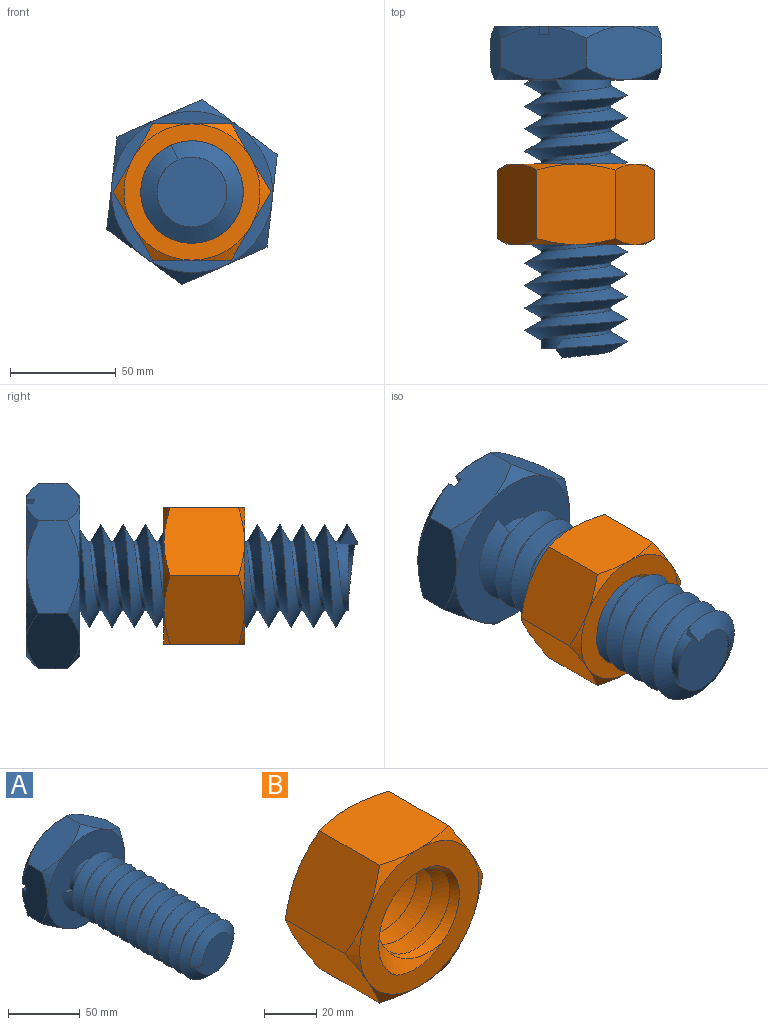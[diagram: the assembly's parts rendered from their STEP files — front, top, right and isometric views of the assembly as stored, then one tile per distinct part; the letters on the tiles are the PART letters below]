
ASSEMBLY  parts=2 mates=1
PART A: 22 faces, bbox 88x156.9x88 mm
  f0: plane 44.01x25.33mm, normal (1,0,0), area 920.4mm2, adj f2,f12,f14,f15,f17,f19,f20,f21
  f1: plane 44.01x25.33mm, normal (-1,0,0), area 920.4mm2, adj f2,f12,f13,f16,f17,f19,f20,f21
  f2: cone r=48.09mm half-angle=45.1deg, axis (0,-1,0), area 332.3mm2, adj f0,f1,f13,f14,f18,f19
  f3: plane 76.05x35.86mm, normal (0,1,0), area 2109.3mm2, adj f17,f20
  f4: plane 76.2x76.2mm, normal (0,-1,0), area 3508.3mm2, adj f5,f8,f10,f12
  f5: cylinder r=16.51mm len=127mm, axis (0,1,0), area 1226.1mm2, adj f4,f6,f8,f9,f10,f11
  f6: plane 33.05x33.05mm, normal (0,-1,0), area 856.5mm2, adj f5,f7
  f7: cylinder r=16.51mm len=31.05mm, axis (0,-1,0), area 97.4mm2, adj f6,f9,f11
  f8: plane 7.7x4.46mm, normal (0,0,1), area 17.2mm2, adj f4,f5,f10,f11
  f9: plane 8.89x7.7mm, normal (0,0,-1), area 34.2mm2, adj f5,f7,f10,f11
  f10: bspline ~131.45x48.39mm, area 13434.1mm2, adj f4,f5,f8,f9,f11
  f11: bspline ~131.45x48.42mm, area 13703.5mm2, adj f5,f7,f8,f9,f10
  f12: cone r=48.09mm half-angle=45.1deg, axis (0,1,0), area 665.1mm2, adj f0,f1,f4,f13,f14,f15,f16
  f13: plane 38.1x25.4mm, normal (-0.5,0,0.87), area 939.1mm2, adj f1,f2,f12,f14
  f14: plane 38.1x25.4mm, normal (0.5,0,0.87), area 939.1mm2, adj f0,f2,f12,f13
  f15: plane 38.1x25.4mm, normal (0.5,0,-0.87), area 939.1mm2, adj f0,f12,f16,f17
  f16: plane 38.1x25.4mm, normal (-0.5,0,-0.87), area 939.1mm2, adj f1,f12,f15,f17
  f17: cone r=48.09mm half-angle=45.1deg, axis (0,-1,0), area 332.4mm2, adj f0,f1,f3,f15,f16,f20
  f18: plane 76x35.48mm, normal (0,1,0), area 2079.9mm2, adj f2,f19
  f19: plane 76.2x3.9mm, normal (0,0,-1), area 297.2mm2, adj f0,f1,f2,f18,f21
  f20: plane 76.2x3.9mm, normal (0,0,1), area 297.2mm2, adj f0,f1,f3,f17,f21
  f21: plane 76.2x4.84mm, normal (0,1,0), area 368.6mm2, adj f0,f1,f19,f20
PART B: 24 faces, bbox 75.1x48.4x75.1 mm
  f0: plane 65.12x65.12mm, normal (0,-1,0), area 1722.1mm2, adj f2,f4,f5,f8,f9,f11,f13,f15
  f1: plane 65.12x65.12mm, normal (0,1,0), area 1722.1mm2, adj f3,f4,f5,f6,f7,f10,f12,f14
  f2: cone r=16.51mm half-angle=45deg, axis (0,-1,0), area 270.1mm2, adj f0,f4,f5
  f3: cone r=21.59mm half-angle=45deg, axis (0,1,0), area 269mm2, adj f1,f4,f5
  f4: bspline ~48.42x48.42mm, area 4574.3mm2, adj f0,f1,f2,f3,f5
  f5: bspline ~48.42x48.42mm, area 4572.2mm2, adj f0,f1,f2,f3,f4
  f6: cone r=56.95mm half-angle=60deg, axis (0,-1,0), area 64.3mm2, adj f1,f18,f23
  f7: cone r=56.95mm half-angle=60deg, axis (0,-1,0), area 64.3mm2, adj f1,f18,f19
  f8: cone r=56.95mm half-angle=60deg, axis (0,1,0), area 64.3mm2, adj f0,f18,f23
  f9: cone r=56.95mm half-angle=60deg, axis (0,1,0), area 64.3mm2, adj f0,f18,f19
  f10: cone r=56.95mm half-angle=60deg, axis (0,-1,0), area 64.3mm2, adj f1,f19,f20
  f11: cone r=56.95mm half-angle=60deg, axis (0,1,0), area 64.3mm2, adj f0,f19,f20
  f12: cone r=56.95mm half-angle=60deg, axis (0,-1,0), area 64.3mm2, adj f1,f20,f21
  f13: cone r=56.95mm half-angle=60deg, axis (0,1,0), area 64.3mm2, adj f0,f20,f21
  f14: cone r=56.95mm half-angle=60deg, axis (0,-1,0), area 64.3mm2, adj f1,f21,f22
  f15: cone r=56.95mm half-angle=60deg, axis (0,1,0), area 64.3mm2, adj f0,f21,f22
  f16: cone r=56.95mm half-angle=60deg, axis (0,-1,0), area 64.3mm2, adj f1,f22,f23
  f17: cone r=56.95mm half-angle=60deg, axis (0,1,0), area 64.3mm2, adj f0,f22,f23
  f18: plane 38.11x32.18mm, normal (0.87,0,0.5), area 1342.3mm2, adj f6,f7,f8,f9,f19,f23
  f19: plane 38.11x32.18mm, normal (0.87,0,-0.5), area 1342.3mm2, adj f7,f9,f10,f11,f18,f20
  f20: plane 38.11x37.17mm, normal (0,0,-1), area 1342.3mm2, adj f10,f11,f12,f13,f19,f21
  f21: plane 38.11x32.18mm, normal (-0.87,0,-0.5), area 1342.3mm2, adj f12,f13,f14,f15,f20,f22
  f22: plane 38.11x32.18mm, normal (-0.87,0,0.5), area 1342.3mm2, adj f14,f15,f16,f17,f21,f23
  f23: plane 38.11x37.17mm, normal (0,0,1), area 1342.3mm2, adj f6,f8,f16,f17,f18,f22
PLACE A rot(axis=(0,1,0),66.3deg) t=(117.31,-196.03,-87.31)mm
PLACE B t=(117.31,-261.23,-87.31)mm fixed
MATE cylindrical A.f5 <-> B.f2  axis (0,-1,0) through (117.31,-348.43,-87.31)mm
